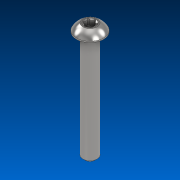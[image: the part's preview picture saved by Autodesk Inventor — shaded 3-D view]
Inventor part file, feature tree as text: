
AUTODESK INVENTOR PART (.ipt)
format: ipt  version: 2022.2 (Build 262287000, 287)  size: 167,424 bytes
history: native  units: in
note: dims shown in document units (in); Inventor stores cm internally (conversion verified against a paired STEP export)
features: direct_edit x1, chamfer x1, move_body x1
ambient origin geometry x8: Origin, YZ Plane, XZ Plane, XY Plane, X Axis, Y Axis, Z Axis, Center Point
bodies: Solid1 (feature_tree)
feature tree (3):
  direct_edit  "Direct Edit1"
  chamfer  "Chamfer2"  [1 undecoded]
  move_body  "Move1"
note: 1 required parameter value undecoded (feature->parameter linkage not recoverable at this tier; creation-order binding heuristic only, values carry confidence <= 0.55)
